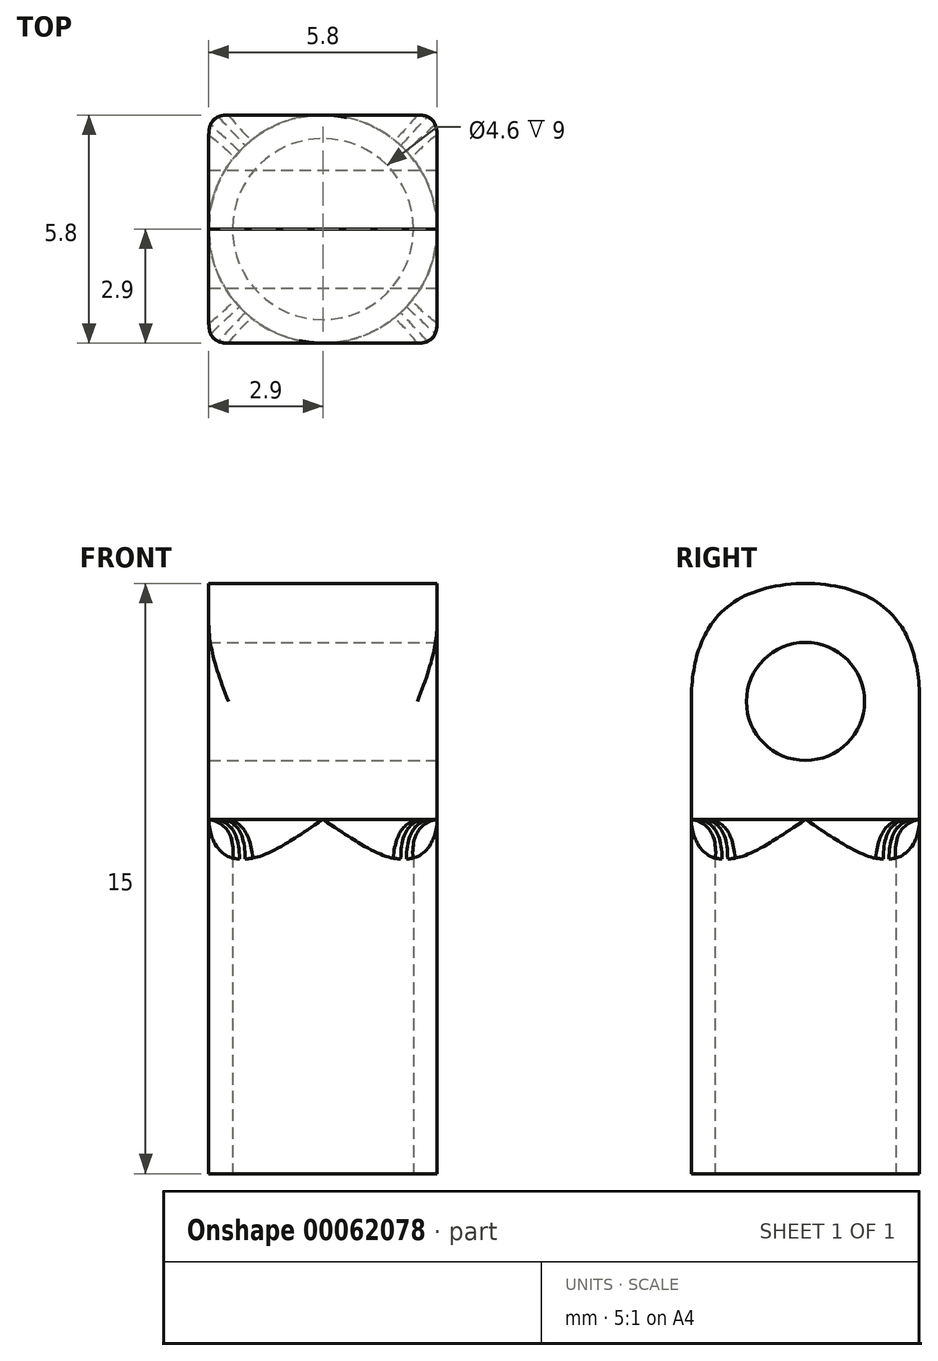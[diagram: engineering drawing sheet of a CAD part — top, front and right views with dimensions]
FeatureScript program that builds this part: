
annotation { "Feature Type Name" : "Feature", "Feature Type Description" : "" }
export const myFeature = defineFeature(function(context is Context, id is Id, definition is map)
    precondition{}
    {
        {
            var Q0;
            Q0=qCreatedBy(makeId("Top.planeOp"),FACE);
            var sketch = newSketch(context, id + "F0", { "sketchPlane" : qUnion([Q0])});
            skCircle(sketch, "E0", {"center": v(0, 0) * mm, "radius": 2.3 * mm});
            skCircle(sketch, "E1", {"center": v(0, 0) * mm, "radius": 2.9 * mm});
            skSolve(sketch);
        }
        {
            var Q0;
            Q0=makeQuery(id+"F0.imprint","IMPRINT",FACE,{"disambiguationData":[TD([[makeQuery(id+"F0.imprint","IMPRINT",EDGE,{"derivedFrom":sQuery(id+"F0.wireOp",EDGE,"E0")}),-1.0]])]});
            extrude(context, id + "F1", {"entities" : qUnion([Q0]), "depth" : 9 * mm});
        }
        {
            var Q0;
            Q0=makeQuery(id+"F1.opExtrude","CAP_FACE",FACE,{"disambiguationData":[OSD([sQuery(id+"F0.wireOp",EDGE,"E0"),sQuery(id+"F0.wireOp",EDGE,"E1")])],"isStart":false});
            var sketch = newSketch(context, id + "F2", { "sketchPlane" : qUnion([Q0])});
            skLineSegment(sketch, "E2.rect.bottom", {"start": v(2.9, 2.9) * mm, "end": v(-2.9, 2.9) * mm});
            skLineSegment(sketch, "E2.rect.top", {"start": v(2.9, -2.9) * mm, "end": v(-2.9, -2.9) * mm});
            skLineSegment(sketch, "E2.rect.left", {"start": v(2.9, 2.9) * mm, "end": v(2.9, -2.9) * mm});
            skLineSegment(sketch, "E2.rect.right", {"start": v(-2.9, 2.9) * mm, "end": v(-2.9, -2.9) * mm});
            skPoint(sketch, "E2.rect.middle", {"position": v(0, 0) * mm});
            skSolve(sketch);
        }
        {
            var Q0;
            Q0=makeQuery(id+"F2.imprint","IMPRINT",FACE,{"disambiguationData":[TD([[makeQuery(id+"F2.imprint","IMPRINT",EDGE,{"derivedFrom":makeQuery(id+"F1.opExtrude","CAP_EDGE",EDGE,{"disambiguationData":[OSD([sQuery(id+"F0.wireOp",EDGE,"E0")])],"isStart":false})}),1.0]])]});
            var Q1;
            {var subQ0=sQuery(id+"F2.wireOp",EDGE,"E2.rect.left");var subQ1=sQuery(id+"F2.wireOp",EDGE,"E2.rect.bottom");var subQ2=makeQuery(id+"F2.imprint","INTERSECT",VERTEX,{"derivedFrom":[subQ1,subQ0]});Q1=makeQuery(id+"F2.imprint","IMPRINT",FACE,{"disambiguationData":[TD([[makeQuery(id+"F2.imprint","IMPRINT",EDGE,{"disambiguationData":[TD([[subQ2,-1.0]])],"derivedFrom":subQ1}),1.0]])]});}
            var Q2;
            {var subQ0=sQuery(id+"F2.wireOp",EDGE,"E2.rect.right");var subQ1=sQuery(id+"F2.wireOp",EDGE,"E2.rect.bottom");var subQ2=makeQuery(id+"F2.imprint","INTERSECT",VERTEX,{"derivedFrom":[subQ1,subQ0]});Q2=makeQuery(id+"F2.imprint","IMPRINT",FACE,{"disambiguationData":[TD([[makeQuery(id+"F2.imprint","IMPRINT",EDGE,{"disambiguationData":[TD([[subQ2,1.0]])],"derivedFrom":subQ1}),1.0]])]});}
            var Q3;
            {var subQ0=sQuery(id+"F2.wireOp",EDGE,"E2.rect.left");var subQ1=sQuery(id+"F2.wireOp",EDGE,"E2.rect.top");var subQ2=makeQuery(id+"F2.imprint","INTERSECT",VERTEX,{"derivedFrom":[subQ1,subQ0]});Q3=makeQuery(id+"F2.imprint","IMPRINT",FACE,{"disambiguationData":[TD([[makeQuery(id+"F2.imprint","IMPRINT",EDGE,{"disambiguationData":[TD([[subQ2,-1.0]])],"derivedFrom":subQ1}),-1.0]])]});}
            var Q4;
            {var subQ0=sQuery(id+"F2.wireOp",EDGE,"E2.rect.right");var subQ1=sQuery(id+"F2.wireOp",EDGE,"E2.rect.top");var subQ2=makeQuery(id+"F2.imprint","INTERSECT",VERTEX,{"derivedFrom":[subQ1,subQ0]});Q4=makeQuery(id+"F2.imprint","IMPRINT",FACE,{"disambiguationData":[TD([[makeQuery(id+"F2.imprint","IMPRINT",EDGE,{"disambiguationData":[TD([[subQ2,1.0]])],"derivedFrom":subQ1}),-1.0]])]});}
            var Q5;
            Q5=makeQuery(id+"F2.imprint","IMPRINT",FACE,{"disambiguationData":[TD([[makeQuery(id+"F2.imprint","IMPRINT",EDGE,{"derivedFrom":makeQuery(id+"F1.opExtrude","CAP_EDGE",EDGE,{"disambiguationData":[OSD([sQuery(id+"F0.wireOp",EDGE,"E0")])],"isStart":false})}),-1.0]])]});
            var Q6;
            Q6=makeQuery(id+"F1.opExtrude","CAP_FACE",FACE,{"disambiguationData":[OSD([sQuery(id+"F0.wireOp",EDGE,"E0"),sQuery(id+"F0.wireOp",EDGE,"E1")])],"isStart":false});
            extrude(context, id + "F3", {"entities" : qUnion([Q0, Q1, Q2, Q3, Q4, Q5, Q6]), "operationType" : NewBodyOperationType.ADD, "depth" : 6 * mm});
        }
        {
            var Q0;
            Q0=makeQuery(id+"F3.opExtrude","SWEPT_FACE",FACE,{"disambiguationData":[OSD([sQuery(id+"F2.wireOp",EDGE,"E2.rect.left")])]});
            var sketch = newSketch(context, id + "F4", { "sketchPlane" : qUnion([Q0])});
            skCircle(sketch, "E3", {"center": v(0, 12) * mm, "radius": 1.35 * mm});
            skSolve(sketch);
        }
        {
            var Q0;
            Q0=sQuery(id+"F4.wireOp",VERTEX,"E3.center");
            var Q1;
            Q1=makeQuery(id+"F1.opExtrude","SWEPT_BODY",BODY,{"disambiguationData":[OSD([sQuery(id+"F0.wireOp",EDGE,"E0"),sQuery(id+"F0.wireOp",EDGE,"E1")])]});
            hole(context, id + "F5", {"style" : HoleStyle.SIMPLE, "holeDiameter" : 3 * mm, "endStyle" : HoleEndStyle.THROUGH, "locations" : qUnion([Q0]), "scope" : qUnion([Q1])});
        }
        {
            var Q0;
            Q0=makeQuery(id+"F3.opExtrude","SWEPT_EDGE",EDGE,{"disambiguationData":[OSD([sQuery(id+"F2.wireOp",EDGE,"E2.rect.bottom"),sQuery(id+"F2.wireOp",EDGE,"E2.rect.right")])]});
            var Q1;
            Q1=makeQuery(id+"F3.opExtrude","SWEPT_EDGE",EDGE,{"disambiguationData":[OSD([sQuery(id+"F2.wireOp",EDGE,"E2.rect.bottom"),sQuery(id+"F2.wireOp",EDGE,"E2.rect.left")])]});
            var Q2;
            Q2=makeQuery(id+"F3.opExtrude","SWEPT_EDGE",EDGE,{"disambiguationData":[OSD([sQuery(id+"F2.wireOp",EDGE,"E2.rect.top"),sQuery(id+"F2.wireOp",EDGE,"E2.rect.right")])]});
            var Q3;
            Q3=makeQuery(id+"F3.opExtrude","SWEPT_EDGE",EDGE,{"disambiguationData":[OSD([sQuery(id+"F2.wireOp",EDGE,"E2.rect.top"),sQuery(id+"F2.wireOp",EDGE,"E2.rect.left")])]});
            var Q4;
            Q4=makeQuery(id+"F5.hole-0.boolean.opBoolean","INTERSECT",EDGE,{"derivedFrom":[makeQuery(id+"F3.opExtrude","SWEPT_FACE",FACE,{"disambiguationData":[OSD([sQuery(id+"F2.wireOp",EDGE,"E2.rect.right")])]}),makeQuery(id+"F5.hole-0.opRevolve","SWEPT_FACE",FACE,{"disambiguationData":[OSD([sQuery(id+"F5.hole-0.sketch.wireOp",EDGE,"core_line_2")])]})]});
            var Q5;
            Q5=makeQuery(id+"F5.hole-0.boolean.opBoolean","COPY",EDGE,{"derivedFrom":makeQuery(id+"F5.hole-0.opRevolve","SWEPT_EDGE",EDGE,{"disambiguationData":[OSD([sQuery(id+"F5.hole-0.sketch.wireOp",EDGE,"core_line_2"),sQuery(id+"F5.hole-0.sketch.wireOp",EDGE,"core_line_3")])]})});
            fillet(context, id + "F6", {"entities" : qUnion([Q0, Q1, Q2, Q3, Q4, Q5]), "radius" : .5 * mm, "tangentPropagation" : true, "rho" : 0.5, "crossSection" : FilletCrossSection.CONIC, "allowEdgeOverflow" : false});
        }
        {
            var Q0;
            {var subQ0=sQuery(id+"F2.wireOp",EDGE,"E2.rect.right");var subQ1=sQuery(id+"F2.wireOp",EDGE,"E2.rect.bottom");var subQ2=sQuery(id+"F0.wireOp",EDGE,"E1");Q0=makeQuery(id+"F3.boolean.opBoolean","SPLIT",EDGE,{"disambiguationData":[TD([makeQuery(id+"F1.opExtrude","SWEPT_FACE",FACE,{"disambiguationData":[OSD([subQ2])]}),makeQuery(id+"F3.opExtrude","CAP_FACE",FACE,{"disambiguationData":[OSD([sQuery(id+"F0.wireOp",EDGE,"E0"),subQ2])],"isStart":true}),makeQuery(id+"F3.opExtrude","SWEPT_FACE",FACE,{"disambiguationData":[OSD([subQ1])]}),makeQuery(id+"F3.opExtrude","CAP_FACE",FACE,{"disambiguationData":[OSD([subQ1,sQuery(id+"F2.wireOp",EDGE,"E2.rect.top"),sQuery(id+"F2.wireOp",EDGE,"E2.rect.left"),subQ0])],"isStart":true}),makeQuery(id+"F3.opExtrude","SWEPT_FACE",FACE,{"disambiguationData":[OSD([subQ0])]})])],"derivedFrom":makeQuery(id+"F1.opExtrude","CAP_EDGE",EDGE,{"disambiguationData":[OSD([subQ2])],"isStart":false})});}
            var Q1;
            {var subQ0=sQuery(id+"F2.wireOp",EDGE,"E2.rect.left");var subQ1=sQuery(id+"F2.wireOp",EDGE,"E2.rect.bottom");var subQ2=sQuery(id+"F0.wireOp",EDGE,"E1");Q1=makeQuery(id+"F3.boolean.opBoolean","SPLIT",EDGE,{"disambiguationData":[TD([makeQuery(id+"F1.opExtrude","SWEPT_FACE",FACE,{"disambiguationData":[OSD([subQ2])]}),makeQuery(id+"F3.opExtrude","CAP_FACE",FACE,{"disambiguationData":[OSD([sQuery(id+"F0.wireOp",EDGE,"E0"),subQ2])],"isStart":true}),makeQuery(id+"F3.opExtrude","SWEPT_FACE",FACE,{"disambiguationData":[OSD([subQ1])]}),makeQuery(id+"F3.opExtrude","CAP_FACE",FACE,{"disambiguationData":[OSD([subQ1,sQuery(id+"F2.wireOp",EDGE,"E2.rect.top"),subQ0,sQuery(id+"F2.wireOp",EDGE,"E2.rect.right")])],"isStart":true}),makeQuery(id+"F3.opExtrude","SWEPT_FACE",FACE,{"disambiguationData":[OSD([subQ0])]})])],"derivedFrom":makeQuery(id+"F1.opExtrude","CAP_EDGE",EDGE,{"disambiguationData":[OSD([subQ2])],"isStart":false})});}
            var Q2;
            {var subQ0=sQuery(id+"F2.wireOp",EDGE,"E2.rect.top");var subQ1=sQuery(id+"F2.wireOp",EDGE,"E2.rect.right");var subQ2=sQuery(id+"F0.wireOp",EDGE,"E1");Q2=makeQuery(id+"F3.boolean.opBoolean","SPLIT",EDGE,{"disambiguationData":[TD([makeQuery(id+"F1.opExtrude","SWEPT_FACE",FACE,{"disambiguationData":[OSD([subQ2])]}),makeQuery(id+"F3.opExtrude","CAP_FACE",FACE,{"disambiguationData":[OSD([sQuery(id+"F0.wireOp",EDGE,"E0"),subQ2])],"isStart":true}),makeQuery(id+"F3.opExtrude","CAP_FACE",FACE,{"disambiguationData":[OSD([sQuery(id+"F2.wireOp",EDGE,"E2.rect.bottom"),subQ0,sQuery(id+"F2.wireOp",EDGE,"E2.rect.left"),subQ1])],"isStart":true}),makeQuery(id+"F3.opExtrude","SWEPT_FACE",FACE,{"disambiguationData":[OSD([subQ0])]}),makeQuery(id+"F3.opExtrude","SWEPT_FACE",FACE,{"disambiguationData":[OSD([subQ1])]})])],"derivedFrom":makeQuery(id+"F1.opExtrude","CAP_EDGE",EDGE,{"disambiguationData":[OSD([subQ2])],"isStart":false})});}
            var Q3;
            {var subQ0=sQuery(id+"F2.wireOp",EDGE,"E2.rect.top");var subQ1=sQuery(id+"F2.wireOp",EDGE,"E2.rect.left");var subQ2=sQuery(id+"F0.wireOp",EDGE,"E1");Q3=makeQuery(id+"F3.boolean.opBoolean","SPLIT",EDGE,{"disambiguationData":[TD([makeQuery(id+"F1.opExtrude","SWEPT_FACE",FACE,{"disambiguationData":[OSD([subQ2])]}),makeQuery(id+"F3.opExtrude","CAP_FACE",FACE,{"disambiguationData":[OSD([sQuery(id+"F0.wireOp",EDGE,"E0"),subQ2])],"isStart":true}),makeQuery(id+"F3.opExtrude","CAP_FACE",FACE,{"disambiguationData":[OSD([sQuery(id+"F2.wireOp",EDGE,"E2.rect.bottom"),subQ0,subQ1,sQuery(id+"F2.wireOp",EDGE,"E2.rect.right")])],"isStart":true}),makeQuery(id+"F3.opExtrude","SWEPT_FACE",FACE,{"disambiguationData":[OSD([subQ0])]}),makeQuery(id+"F3.opExtrude","SWEPT_FACE",FACE,{"disambiguationData":[OSD([subQ1])]})])],"derivedFrom":makeQuery(id+"F1.opExtrude","CAP_EDGE",EDGE,{"disambiguationData":[OSD([subQ2])],"isStart":false})});}
            fillet(context, id + "F7", {"entities" : qUnion([Q0, Q1, Q2, Q3]), "radius" : 1 * mm, "tangentPropagation" : true, "rho" : 0.5, "crossSection" : FilletCrossSection.CONIC, "allowEdgeOverflow" : false});
        }
        {
            var Q0;
            Q0=makeQuery(id+"F3.opExtrude","CAP_EDGE",EDGE,{"disambiguationData":[OSD([sQuery(id+"F2.wireOp",EDGE,"E2.rect.top")])],"isStart":false});
            var Q1;
            Q1=makeQuery(id+"F3.opExtrude","CAP_EDGE",EDGE,{"disambiguationData":[OSD([sQuery(id+"F2.wireOp",EDGE,"E2.rect.bottom")])],"isStart":false});
            fillet(context, id + "F8", {"entities" : qUnion([Q0, Q1]), "radius" : 3 * mm, "rho" : 0.5, "crossSection" : FilletCrossSection.CONIC, "allowEdgeOverflow" : false});
        }
    });
